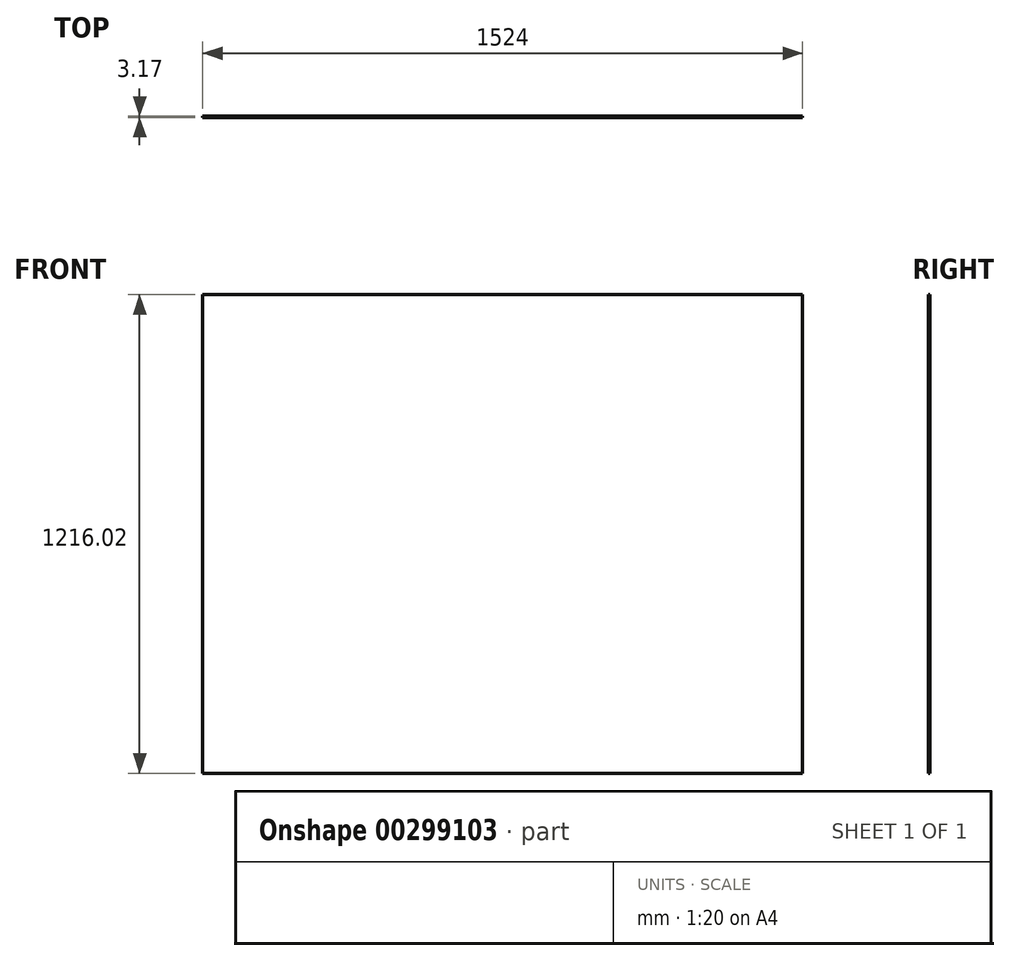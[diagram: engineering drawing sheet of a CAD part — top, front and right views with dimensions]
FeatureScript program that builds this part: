
annotation { "Feature Type Name" : "Feature", "Feature Type Description" : "" }
export const myFeature = defineFeature(function(context is Context, id is Id, definition is map)
    precondition{}
    {
        {
            var Q0;
            Q0=qCreatedBy(makeId("Front.planeOp"),FACE);
            var sketch = newSketch(context, id + "F0", { "sketchPlane" : qUnion([Q0])});
            skLineSegment(sketch, "E0.bottom", {"start": v(762, 608.01) * mm, "end": v(-762, 608.01) * mm});
            skLineSegment(sketch, "E0.top", {"start": v(762, -608.01) * mm, "end": v(-762, -608.01) * mm});
            skLineSegment(sketch, "E0.left", {"start": v(762, 608.01) * mm, "end": v(762, -608.01) * mm});
            skLineSegment(sketch, "E0.right", {"start": v(-762, 608.01) * mm, "end": v(-762, -608.01) * mm});
            skPoint(sketch, "E0.middle", {"position": v(0, 0) * mm});
            skSolve(sketch);
        }
        {
            var Q0;
            Q0 = qSketchRegion(id + "F0", true);
            extrude(context, id + "F1", {"entities" : qUnion([Q0]), "depth" : 3.17 * mm});
        }
    });
